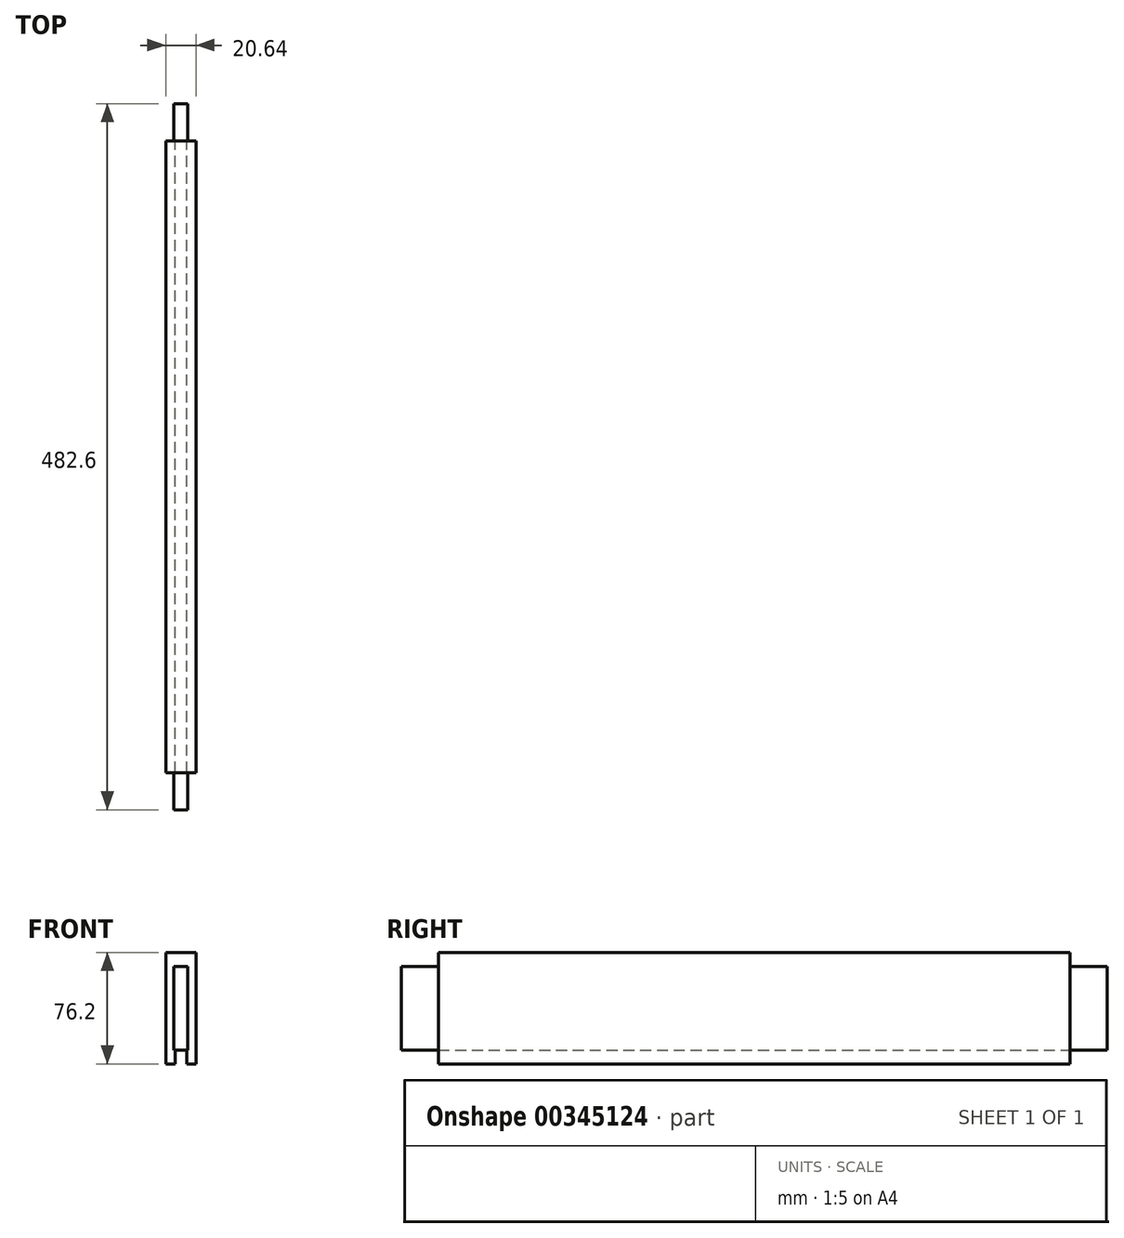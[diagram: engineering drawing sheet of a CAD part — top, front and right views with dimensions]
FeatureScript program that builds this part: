
annotation { "Feature Type Name" : "Feature", "Feature Type Description" : "" }
export const myFeature = defineFeature(function(context is Context, id is Id, definition is map)
    precondition{}
    {
        {
            var Q0;
            Q0=qCreatedBy(makeId("Right.planeOp"),FACE);
            var sketch = newSketch(context, id + "F0", { "sketchPlane" : qUnion([Q0])});
            skLineSegment(sketch, "E0.bottom", {"start": v(-215.9, 38.1) * mm, "end": v(215.9, 38.1) * mm});
            skLineSegment(sketch, "E0.top", {"start": v(-215.9, -38.1) * mm, "end": v(215.9, -38.1) * mm});
            skLineSegment(sketch, "E0.left", {"start": v(-215.9, 38.1) * mm, "end": v(-215.9, -38.1) * mm});
            skLineSegment(sketch, "E0.right", {"start": v(215.9, 38.1) * mm, "end": v(215.9, -38.1) * mm});
            skPoint(sketch, "E0.middle", {"position": v(0, 0) * mm});
            skSolve(sketch);
        }
        {
            var Q0;
            Q0 = qSketchRegion(id + "F0", true);
            extrude(context, id + "F1", {"entities" : qUnion([Q0]), "endBound" : BoundingType.SYMMETRIC, "depth" : 20.64 * mm});
        }
        {
            var Q0;
            Q0=makeQuery(id+"F1.opExtrude","SWEPT_FACE",FACE,{"disambiguationData":[OSD([sQuery(id+"F0.wireOp",EDGE,"E0.left")])]});
            var sketch = newSketch(context, id + "F2", { "sketchPlane" : qUnion([Q0])});
            skLineSegment(sketch, "E1.bottom", {"start": v(-4.76, 28.57) * mm, "end": v(4.76, 28.57) * mm});
            skLineSegment(sketch, "E1.top", {"start": v(-4.76, -28.57) * mm, "end": v(4.76, -28.57) * mm});
            skLineSegment(sketch, "E1.left", {"start": v(-4.76, 28.57) * mm, "end": v(-4.76, -28.57) * mm});
            skLineSegment(sketch, "E1.right", {"start": v(4.76, 28.57) * mm, "end": v(4.76, -28.57) * mm});
            skPoint(sketch, "E1.middle", {"position": v(0, 0) * mm});
            skSolve(sketch);
        }
        {
            var Q0;
            Q0 = qSketchRegion(id + "F2", true);
            extrude(context, id + "F3", {"entities" : qUnion([Q0]), "operationType" : NewBodyOperationType.ADD, "depth" : 25.4 * mm});
        }
        {
            var Q0;
            Q0=makeQuery(id+"F1.opExtrude","SWEPT_FACE",FACE,{"disambiguationData":[OSD([sQuery(id+"F0.wireOp",EDGE,"E0.right")])]});
            var sketch = newSketch(context, id + "F4", { "sketchPlane" : qUnion([Q0])});
            skLineSegment(sketch, "E2.bottom", {"start": v(-4.76, 28.58) * mm, "end": v(4.76, 28.58) * mm});
            skLineSegment(sketch, "E2.top", {"start": v(-4.76, -28.58) * mm, "end": v(4.76, -28.58) * mm});
            skLineSegment(sketch, "E2.left", {"start": v(-4.76, 28.58) * mm, "end": v(-4.76, -28.58) * mm});
            skLineSegment(sketch, "E2.right", {"start": v(4.76, 28.58) * mm, "end": v(4.76, -28.58) * mm});
            skPoint(sketch, "E2.middle", {"position": v(0, 0) * mm});
            skSolve(sketch);
        }
        {
            var Q0;
            Q0 = qSketchRegion(id + "F4", true);
            extrude(context, id + "F5", {"entities" : qUnion([Q0]), "operationType" : NewBodyOperationType.ADD, "depth" : 25.4 * mm});
        }
        {
            var Q0;
            Q0=makeQuery(id+"F1.opExtrude","SWEPT_FACE",FACE,{"disambiguationData":[OSD([sQuery(id+"F0.wireOp",EDGE,"E0.top")])]});
            var sketch = newSketch(context, id + "F6", { "sketchPlane" : qUnion([Q0])});
            skLineSegment(sketch, "E3.bottom", {"start": v(3.97, 215.9) * mm, "end": v(-3.97, 215.9) * mm});
            skLineSegment(sketch, "E3.top", {"start": v(3.97, -215.9) * mm, "end": v(-3.97, -215.9) * mm});
            skLineSegment(sketch, "E3.left", {"start": v(3.97, 215.9) * mm, "end": v(3.97, -215.9) * mm});
            skLineSegment(sketch, "E3.right", {"start": v(-3.97, 215.9) * mm, "end": v(-3.97, -215.9) * mm});
            skPoint(sketch, "E3.middle", {"position": v(0, 0) * mm});
            skSolve(sketch);
        }
        {
            var Q0;
            Q0=makeQuery(id+"F6.imprint","IMPRINT",FACE,{"disambiguationData":[TD([[makeQuery(id+"F6.imprint","IMPRINT",EDGE,{"derivedFrom":sQuery(id+"F6.wireOp",EDGE,"E3.bottom")}),1.0]])]});
            extrude(context, id + "F7", {"entities" : qUnion([Q0]), "operationType" : NewBodyOperationType.REMOVE, "oppositeDirection" : true, "depth" : 9.52 * mm});
        }
    });
